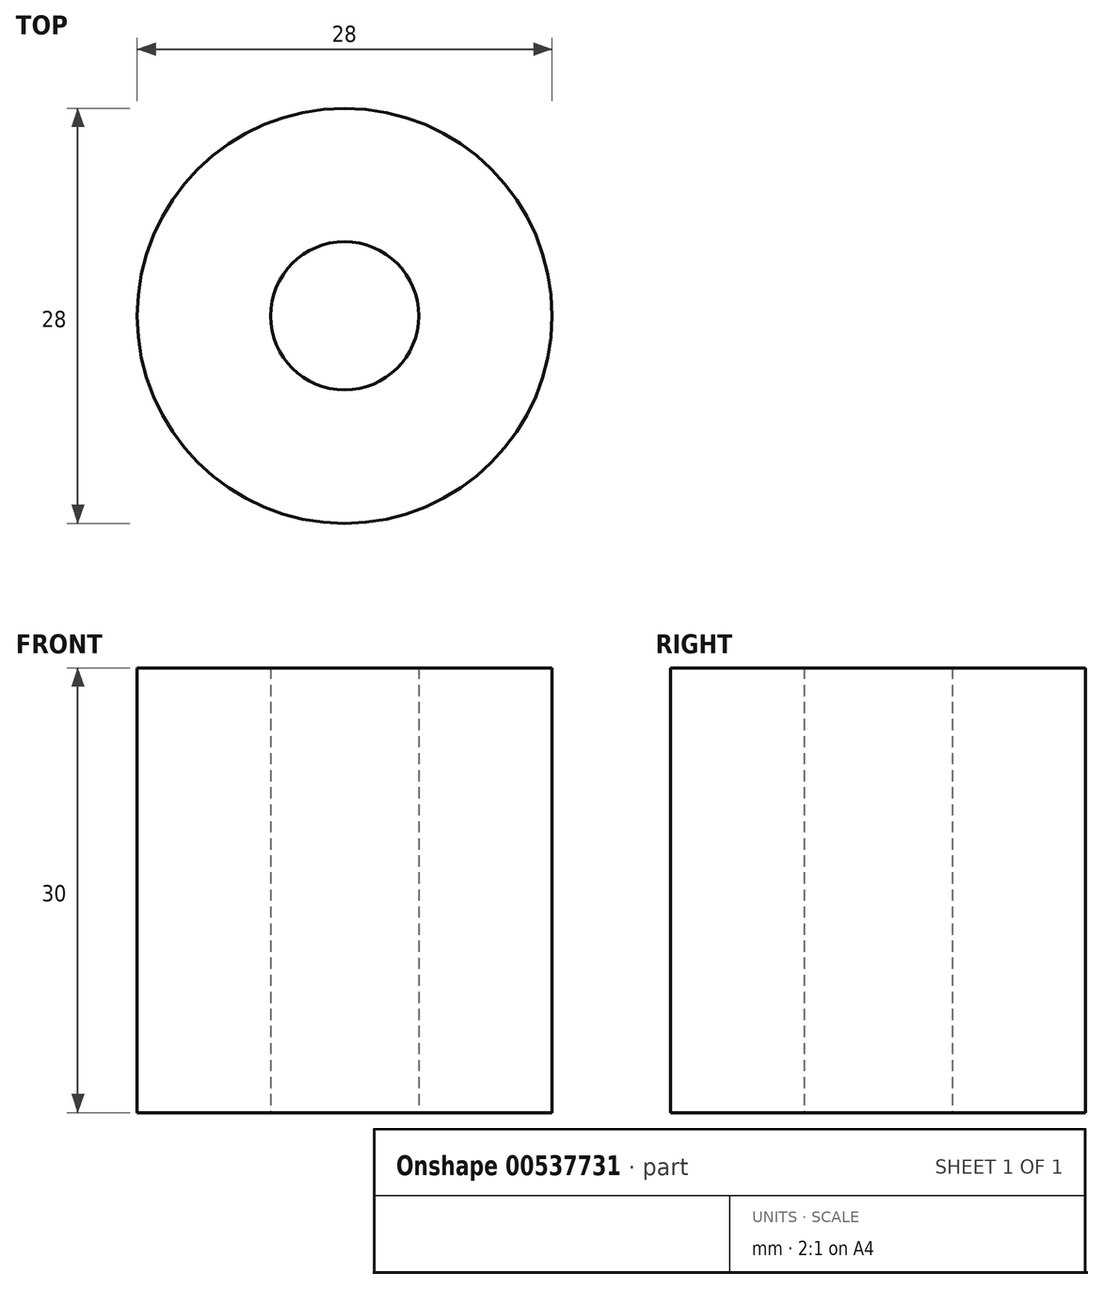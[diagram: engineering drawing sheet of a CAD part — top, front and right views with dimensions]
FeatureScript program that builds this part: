
annotation { "Feature Type Name" : "Feature", "Feature Type Description" : "" }
export const myFeature = defineFeature(function(context is Context, id is Id, definition is map)
    precondition{}
    {
        {
            var Q0;
            Q0=qCreatedBy(makeId("Top.planeOp"),FACE);
            var sketch = newSketch(context, id + "F0", { "sketchPlane" : qUnion([Q0])});
            skCircle(sketch, "E0", {"center": v(0, 0) * mm, "radius": 5 * mm});
            skCircle(sketch, "E1", {"center": v(0, 0) * mm, "radius": 14 * mm});
            skSolve(sketch);
        }
        {
            var Q0;
            Q0=makeQuery(id+"F0.imprint","IMPRINT",FACE,{"disambiguationData":[TD([[makeQuery(id+"F0.imprint","IMPRINT",EDGE,{"derivedFrom":sQuery(id+"F0.wireOp",EDGE,"E0")}),-1.0]])]});
            extrude(context, id + "F1", {"entities" : qUnion([Q0]), "depth" : 30 * mm, "offsetDistance" : 25 * mm});
        }
    });
